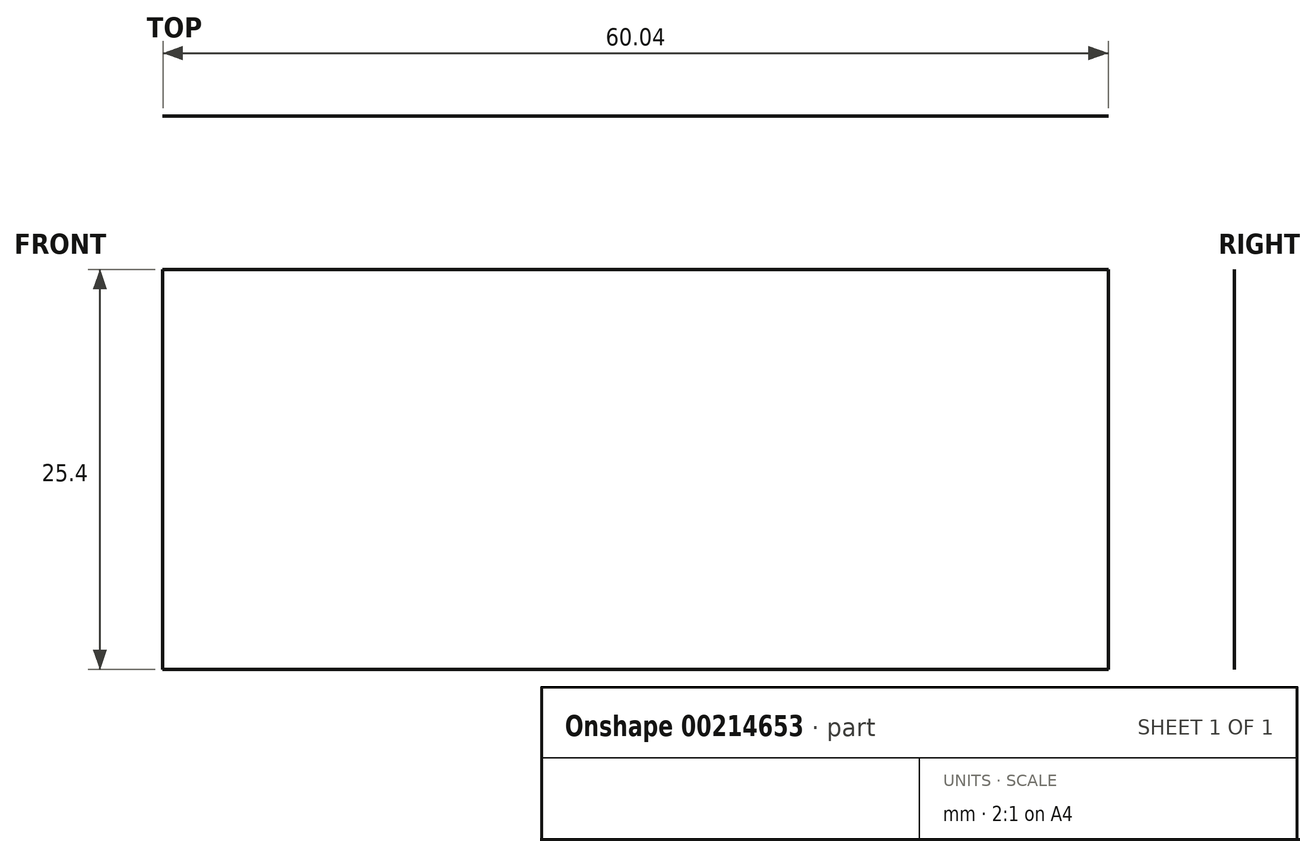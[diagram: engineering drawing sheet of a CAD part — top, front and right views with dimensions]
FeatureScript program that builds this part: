
annotation { "Feature Type Name" : "Feature", "Feature Type Description" : "" }
export const myFeature = defineFeature(function(context is Context, id is Id, definition is map)
    precondition{}
    {
        {
            var Q0;
            Q0=qCreatedBy(makeId("Top.planeOp"),FACE);
            var sketch = newSketch(context, id + "F0", { "sketchPlane" : qUnion([Q0])});
            skLineSegment(sketch, "E0.bottom", {"start": v(-64.12, 62.52) * mm, "end": v(-4.08, 62.52) * mm});
            skLineSegment(sketch, "E0.top", {"start": v(-64.12, -52.32) * mm, "end": v(-4.08, -52.32) * mm});
            skLineSegment(sketch, "E0.left", {"start": v(-64.12, 62.52) * mm, "end": v(-64.12, -52.32) * mm});
            skLineSegment(sketch, "E0.right", {"start": v(-4.08, 62.52) * mm, "end": v(-4.08, -52.32) * mm});
            skCircle(sketch, "E1", {"center": v(33.23, 35.12) * mm, "radius": 29.27 * mm});
            skSolve(sketch);
        }
        {
            var Q0;
            Q0=sQuery(id+"F0.wireOp",EDGE,"E0.bottom");
            extrude(context, id + "F1", {"bodyType" : ToolBodyType.SURFACE, "surfaceEntities" : qUnion([Q0]), "depth" : 25.4 * mm});
        }
    });
